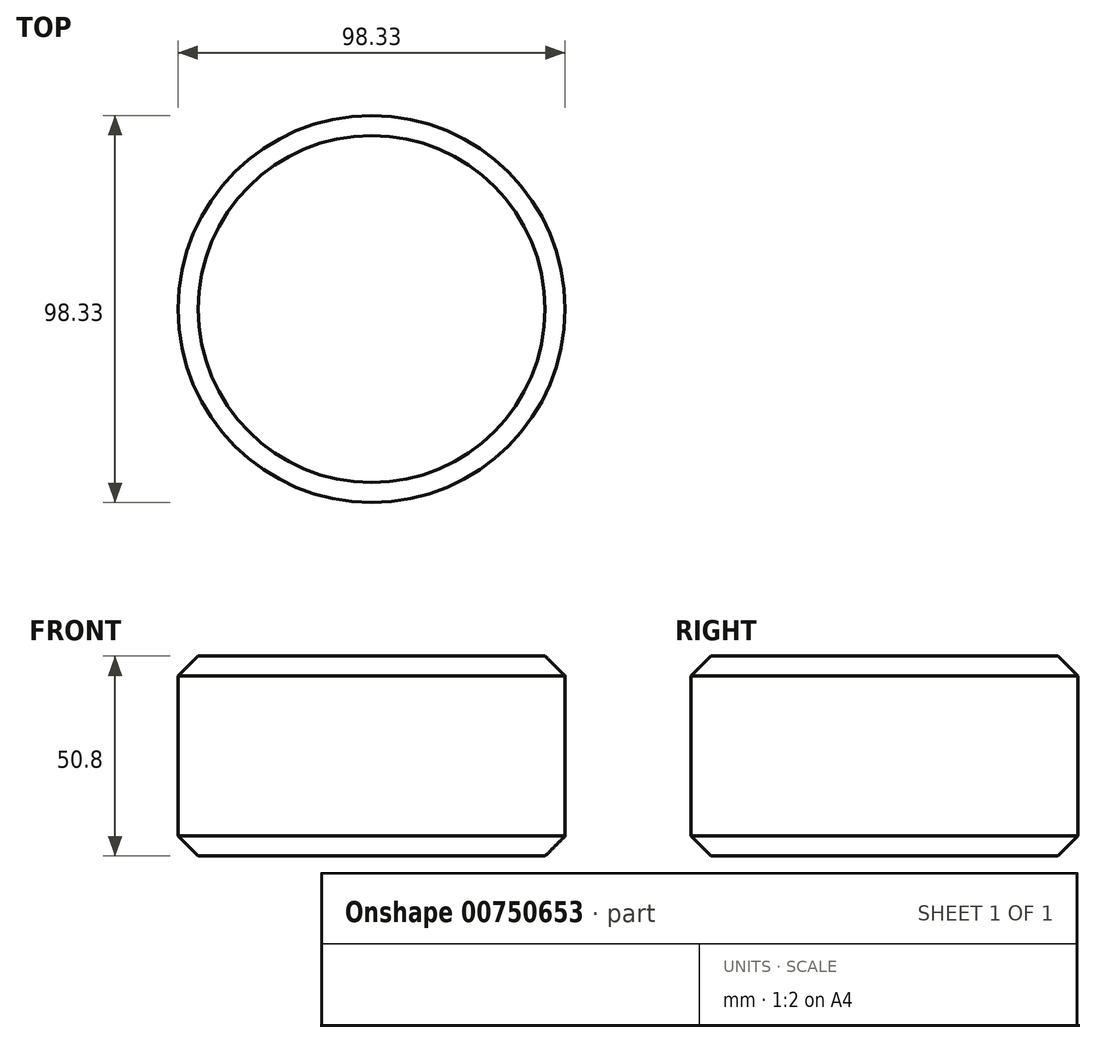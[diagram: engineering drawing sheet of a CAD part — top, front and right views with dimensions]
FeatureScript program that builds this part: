
annotation { "Feature Type Name" : "Feature", "Feature Type Description" : "" }
export const myFeature = defineFeature(function(context is Context, id is Id, definition is map)
    precondition{}
    {
        {
            var Q0;
            Q0=qCreatedBy(makeId("Top.planeOp"),FACE);
            var sketch = newSketch(context, id + "F0", { "sketchPlane" : qUnion([Q0])});
            skCircle(sketch, "E0", {"center": v(-1.98, 7.35) * mm, "radius": 49.17 * mm});
            skPoint(sketch, "E0.first.point", {"position": v(-38.33, 40.46) * mm});
            skPoint(sketch, "E0.second.point", {"position": v(29.16, -30.7) * mm});
            skPoint(sketch, "E0.third.point", {"position": v(45.35, -5.95) * mm});
            skSolve(sketch);
        }
        {
            var Q0;
            Q0 = qSketchRegion(id + "F0", true);
            extrude(context, id + "F1", {"entities" : qUnion([Q0]), "depth" : 50.8 * mm, "offsetDistance" : 25.4 * mm});
        }
        {
            var Q0;
            Q0=makeQuery(id+"F1.opExtrude","CAP_FACE",FACE,{"disambiguationData":[OSD([sQuery(id+"F0.wireOp",EDGE,"E0")])],"isStart":false});
            var sketch = newSketch(context, id + "F2", { "sketchPlane" : qUnion([Q0])});
            skSolve(sketch);
        }
        {
            var Q0;
            Q0=makeQuery(id+"F1.opExtrude","SWEPT_FACE",FACE,{"disambiguationData":[OSD([sQuery(id+"F0.wireOp",EDGE,"E0")])]});
            chamfer(context, id + "F3", {"entities" : qUnion([Q0]), "width" : 5.08 * mm, "tangentPropagation" : true});
        }
    });
